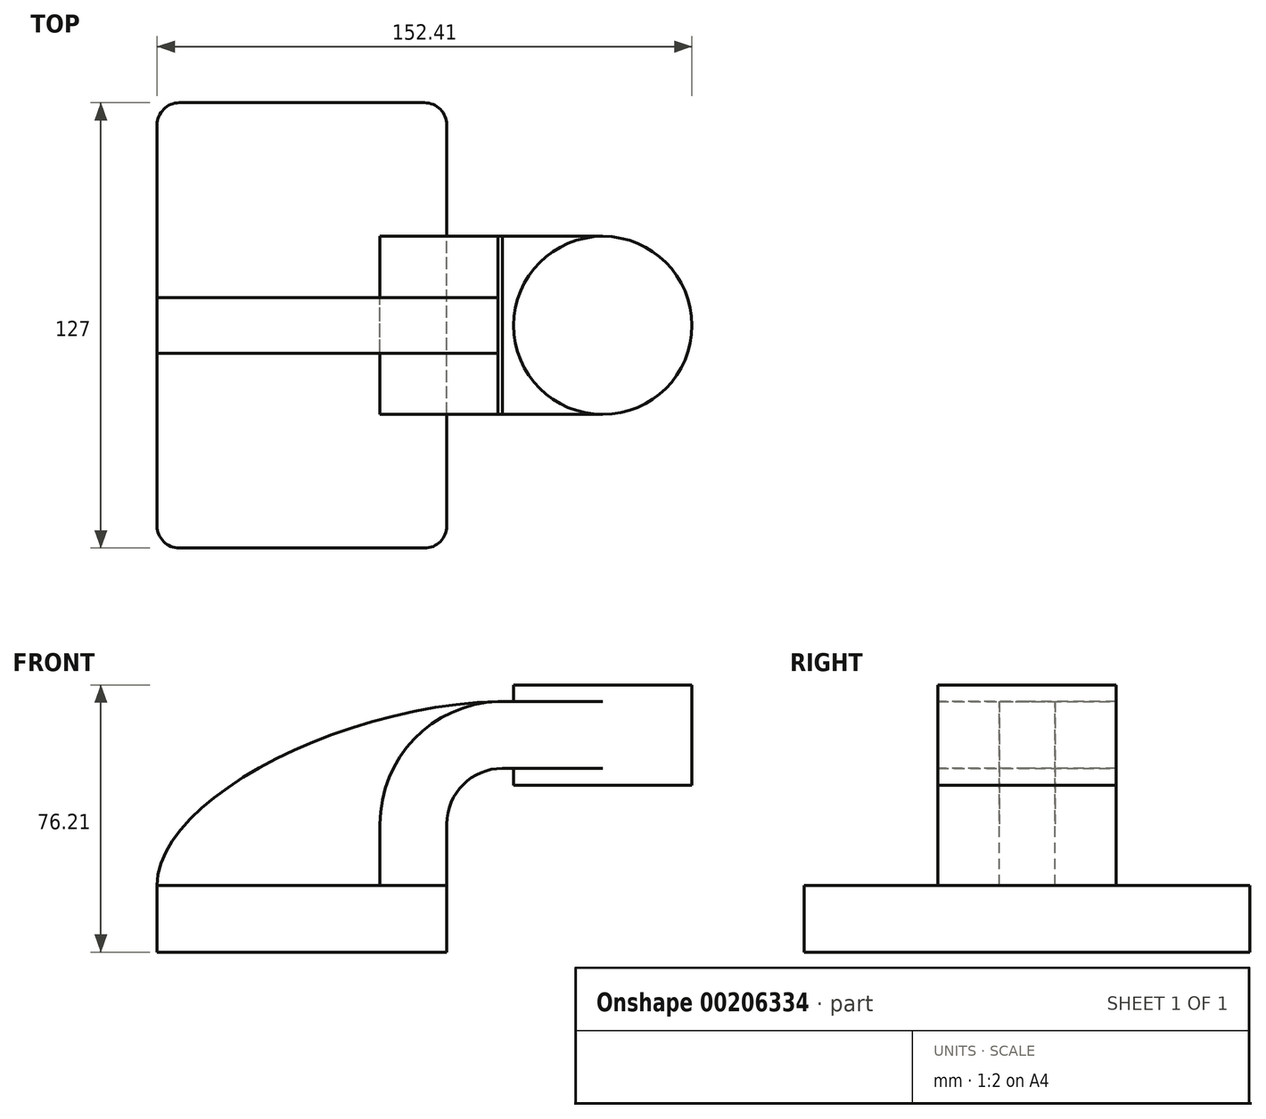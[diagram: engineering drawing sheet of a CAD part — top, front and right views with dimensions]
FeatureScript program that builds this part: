
annotation { "Feature Type Name" : "Feature", "Feature Type Description" : "" }
export const myFeature = defineFeature(function(context is Context, id is Id, definition is map)
    precondition{}
    {
        {
            var Q0;
            Q0=qCreatedBy(makeId("Front.planeOp"),FACE);
            var sketch = newSketch(context, id + "F0", { "sketchPlane" : qUnion([Q0])});
            skLineSegment(sketch, "E0.bottom", {"start": v(-41.28, -9.53) * mm, "end": v(41.28, -9.53) * mm});
            skLineSegment(sketch, "E0.top", {"start": v(-41.28, 9.53) * mm, "end": v(41.28, 9.53) * mm});
            skLineSegment(sketch, "E0.left", {"start": v(-41.28, -9.53) * mm, "end": v(-41.28, 9.53) * mm});
            skLineSegment(sketch, "E0.right", {"start": v(41.28, -9.53) * mm, "end": v(41.28, 9.53) * mm});
            skPoint(sketch, "E0.middle", {"position": v(0, 0) * mm});
            skLineSegment(sketch, "E1.bottom", {"start": v(60.32, 38.1) * mm, "end": v(111.12, 38.1) * mm});
            skLineSegment(sketch, "E1.top", {"start": v(60.32, 66.68) * mm, "end": v(111.12, 66.68) * mm});
            skLineSegment(sketch, "E1.left", {"start": v(60.32, 38.1) * mm, "end": v(60.32, 66.68) * mm});
            skLineSegment(sketch, "E1.right", {"start": v(111.12, 38.1) * mm, "end": v(111.12, 66.68) * mm});
            skPoint(sketch, "E1.middle", {"position": v(85.72, 52.39) * mm});
            skLineSegment(sketch, "E2", {"start": v(41.28, 9.53) * mm, "end": v(41.28, 27) * mm});
            skArc(sketch, "E3", {"start": v(41.27, 27) * mm, "mid": v(45.92, 38.23) * mm, "end": v(57.15, 42.88) * mm});
            skLineSegment(sketch, "E4", {"start": v(57.15, 42.88) * mm, "end": v(85.72, 42.88) * mm});
            skLineSegment(sketch, "E5.0", {"start": v(57.15, 61.93) * mm, "end": v(85.72, 61.93) * mm});
            skArc(sketch, "E5.1", {"start": v(22.23, 27) * mm, "mid": v(32.45, 51.7) * mm, "end": v(57.15, 61.93) * mm});
            skLineSegment(sketch, "E5.2", {"start": v(22.22, 9.53) * mm, "end": v(22.22, 27) * mm});
            skLineSegment(sketch, "E6", {"start": v(85.72, 38.1) * mm, "end": v(85.72, 66.68) * mm});
            skFitSpline(sketch, "E7", {"points": [v(-41.28, 9.53) * mm, v(57.15, 61.93) * mm], "startDerivative": vector(-0.45, 72.77) * mm, "endDerivative": vector(137.03, 1.76) * mm});
            skSolve(sketch);
        }
        {
            var Q0;
            Q0=makeQuery(id+"F0.imprint","IMPRINT",FACE,{"disambiguationData":[TD([[makeQuery(id+"F0.imprint","IMPRINT",EDGE,{"derivedFrom":sQuery(id+"F0.wireOp",EDGE,"E0.bottom")}),1.0]])]});
            extrude(context, id + "F1", {"entities" : qUnion([Q0]), "endBound" : BoundingType.SYMMETRIC, "depth" : 127 * mm});
        }
        {
            var Q0;
            {var subQ1=sQuery(id+"F0.wireOp",EDGE,"E2");Q0=makeQuery(id+"F0.imprint","IMPRINT",FACE,{"disambiguationData":[TD([[makeQuery(id+"F0.imprint","IMPRINT",EDGE,{"derivedFrom":subQ1}),1.0]])]});}
            var Q1;
            {var subQ0=sQuery(id+"F0.wireOp",EDGE,"E4");var subQ1=sQuery(id+"F0.wireOp",EDGE,"E1.left");var subQ2=makeQuery(id+"F0.imprint","INTERSECT",VERTEX,{"derivedFrom":[subQ1,subQ0]});Q1=makeQuery(id+"F0.imprint","IMPRINT",FACE,{"disambiguationData":[TD([[makeQuery(id+"F0.imprint","IMPRINT",EDGE,{"disambiguationData":[TD([[subQ2,-1.0]])],"derivedFrom":subQ1}),-1.0]])]});}
            extrude(context, id + "F2", {"entities" : qUnion([Q0, Q1]), "endBound" : BoundingType.SYMMETRIC, "depth" : 50.8 * mm});
        }
        {
            var Q0;
            {var subQ3=sQuery(id+"F0.wireOp",EDGE,"E5.2");Q0=makeQuery(id+"F0.imprint","IMPRINT",FACE,{"disambiguationData":[TD([[makeQuery(id+"F0.imprint","IMPRINT",EDGE,{"derivedFrom":subQ3}),1.0]])]});}
            extrude(context, id + "F3", {"entities" : qUnion([Q0]), "endBound" : BoundingType.SYMMETRIC, "depth" : 15.88 * mm});
        }
        {
            var Q0;
            {var subQ0=sQuery(id+"F0.wireOp",EDGE,"E1.right");Q0=makeQuery(id+"F0.imprint","IMPRINT",FACE,{"disambiguationData":[TD([[makeQuery(id+"F0.imprint","IMPRINT",EDGE,{"derivedFrom":subQ0}),1.0]])]});}
            var Q1;
            Q1=sQuery(id+"F0.wireOp",EDGE,"E6");
            revolve(context, id + "F4", {"operationType" : NewBodyOperationType.ADD, "entities" : qUnion([Q0]), "axis" : qUnion([Q1]), "revolveType" : RevolveType.FULL});
        }
        {
            var Q0;
            Q0=makeQuery(id+"F1.opExtrude","CAP_EDGE",EDGE,{"disambiguationData":[OSD([sQuery(id+"F0.wireOp",EDGE,"E0.right")])],"isStart":false});
            var Q1;
            Q1=makeQuery(id+"F1.opExtrude","CAP_EDGE",EDGE,{"disambiguationData":[OSD([sQuery(id+"F0.wireOp",EDGE,"E0.left")])],"isStart":false});
            var Q2;
            Q2=makeQuery(id+"F1.opExtrude","CAP_EDGE",EDGE,{"disambiguationData":[OSD([sQuery(id+"F0.wireOp",EDGE,"E0.right")])],"isStart":true});
            var Q3;
            Q3=makeQuery(id+"F1.opExtrude","CAP_EDGE",EDGE,{"disambiguationData":[OSD([sQuery(id+"F0.wireOp",EDGE,"E0.left")])],"isStart":true});
            fillet(context, id + "F5", {"entities" : qUnion([Q0, Q1, Q2, Q3]), "radius" : 6.35 * mm, "tangentPropagation" : true, "allowEdgeOverflow" : false});
        }
    });
